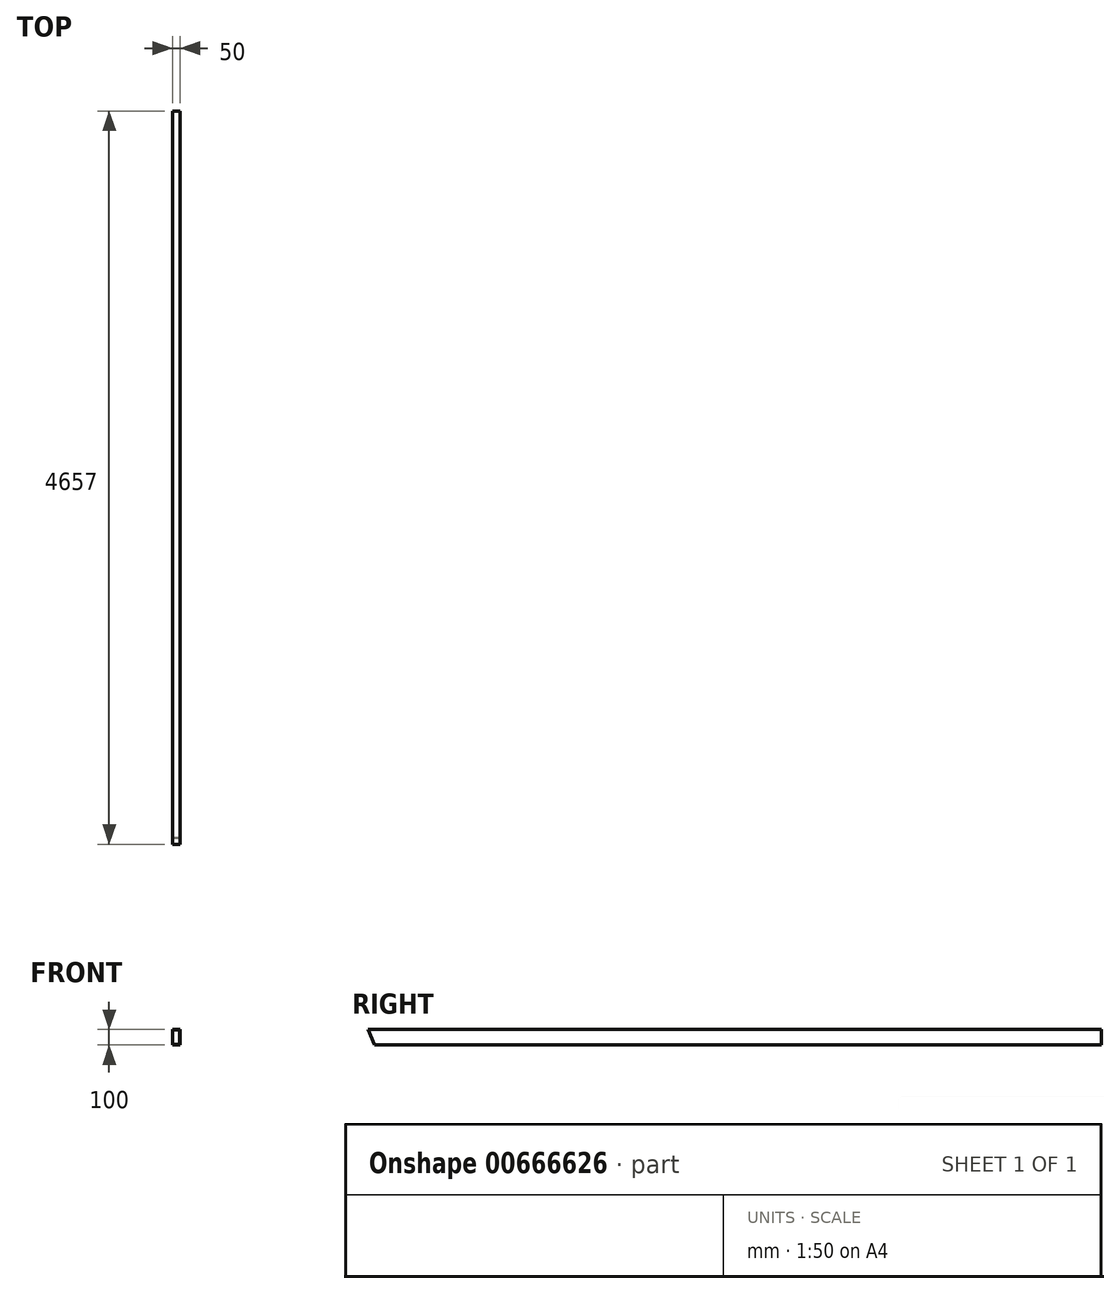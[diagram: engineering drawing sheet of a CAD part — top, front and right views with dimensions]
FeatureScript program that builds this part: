
annotation { "Feature Type Name" : "Feature", "Feature Type Description" : "" }
export const myFeature = defineFeature(function(context is Context, id is Id, definition is map)
    precondition{}
    {
        {
            var Q0;
            Q0=qCreatedBy(makeId("Front.planeOp"),FACE);
            var sketch = newSketch(context, id + "F0", { "sketchPlane" : qUnion([Q0])});
            skLineSegment(sketch, "E0.bottom", {"start": v(25, -50) * mm, "end": v(-25, -50) * mm});
            skLineSegment(sketch, "E0.top", {"start": v(25, 50) * mm, "end": v(-25, 50) * mm});
            skLineSegment(sketch, "E0.left", {"start": v(25, -50) * mm, "end": v(25, 50) * mm});
            skLineSegment(sketch, "E0.right", {"start": v(-25, -50) * mm, "end": v(-25, 50) * mm});
            skPoint(sketch, "E0.middle", {"position": v(0, 0) * mm});
            skLineSegment(sketch, "E1.bottom", {"start": v(22, -47) * mm, "end": v(-22, -47) * mm});
            skLineSegment(sketch, "E1.top", {"start": v(22, 47) * mm, "end": v(-22, 47) * mm});
            skLineSegment(sketch, "E1.left", {"start": v(22, -47) * mm, "end": v(22, 47) * mm});
            skLineSegment(sketch, "E1.right", {"start": v(-22, -47) * mm, "end": v(-22, 47) * mm});
            skSolve(sketch);
        }
        {
            var Q0;
            Q0=makeQuery(id+"F0.imprint","IMPRINT",FACE,{"disambiguationData":[TD([[makeQuery(id+"F0.imprint","IMPRINT",EDGE,{"derivedFrom":sQuery(id+"F0.wireOp",EDGE,"E0.bottom")}),-1.0]])]});
            extrude(context, id + "F1", {"entities" : qUnion([Q0]), "depth" : 4657 * mm, "offsetDistance" : 25 * mm});
        }
        {
            var Q0;
            Q0=makeQuery(id+"F1.opExtrude","CAP_EDGE",EDGE,{"disambiguationData":[OSD([sQuery(id+"F0.wireOp",EDGE,"E0.bottom")])],"isStart":false});
            chamfer(context, id + "F2", {"entities" : qUnion([Q0]), "chamferType" : ChamferType.TWO_OFFSETS, "width1" : 41 * mm, "oppositeDirection" : false, "width2" : 100 * mm, "tangentPropagation" : true});
        }
    });
